# Revit family: NBS_DudleyIndustriesLimited_HndDryrs_ModuloSlimlineBehindTheMirrorHandHygieneSystemHandDryer
name_source: partatom
category: Specialty Equipment
units: mm (PartAtom-declared; Revit-internal decimal feet)

## family parameters
Always vertical = Yes
Cut with Voids When Loaded = No
Part Type = Normal
Room Calculation Point = No
Round Connector Dimension = Use Diameter
Shared = No
Work Plane-Based = No

## types (1)
- Modulo Slimline Behind The Mirror Hand Hygiene System Hand Dryer
    Accessories = Not required.,92405BK, Modulo Slimline Base Shelf, 600 mm.,92404BK,  Modulo Slimline Base Shelf, 1200 mm
    AssetType = Fixed
    BIMObjectName = NBS_DudleyIndustriesLimited_HandDryers_ModuloSlimlineBehindTheMirrorHandHygieneSystemHandDryer
    BlankingPlates = Not required.,Required
    BodyColour = Matte black
    BodyDimensions = 388 x 328 x 173 mm
    BodyFinish = Powder coated
    BodyMaterial = Stainless steel
    Category = Pr_40_70_62_37:Hand dryers
    Color = Black
    Description = Hand dryer
    DurationUnit = year
    ElectricalSupplyFrequency = 50/60 Hz
    ElectricalSupplyPowerRating = 1.7 kW
    ElectricalSupplyRatedOperationalVoltageUe = 230 V a.c
    Features = Hands only
    Finish = Powder-coated
    Form = Warm air
    HandDryerDepth = 173 mm
    HandDryerHeight = 328 mm  [stored 1.07612 ft]
    HandDryerMaterial = NBS_DudleyIndustriesLimited_StainlessSteel_MatteBlackPowderCoated
    HandDryerWidth = 388 mm  [stored 1.27297 ft]
    IfcExportAs = IfcElectricApplianceType
    IfcExportType = HANDDRYER
    ManufacturerName = Dudley Industries Limited
    ManufacturerURL = www.dudleyindustries.com
    Material = Stainless steel
    ModelReference = ModuloSlimlineBehindTheMirrorHandHygieneSystem, HandDryer
    NBSCertification = www.nationalbimlibrary.com/cert/d02wqjjd
    Name = HandDryers_ModuloSlimlineBehindTheMirrorHandHygieneSystem, HandDryer_DudleyIndustriesLimited
    NoiseLevelAt1MMaximum = 71 dB(A)
    NominalHeight = 328 mm  [stored 1.07612 ft]
    NominalLength = 0 mm  [stored 0 ft]
    NominalWidth = 388 mm  [stored 1.27297 ft]
    Operation = Automatic
    Sensors = 100 mm range
    Shape = Rectangle
    Size = 388 x 328 x 173 mm
    ThirdPartyAccreditation = CE marked
    Uniclass2015Code = Pr_40_70_62_37
    Uniclass2015Title = Hand dryers
    Uniclass2015Version = Products v1.22
    Velocity = 28 m/s
    Version = 1
    WarrantyDescription = Three year
    WarrantyDurationParts = Three year
    WarrantyDurationUnit = year
    Weight = 6.5 kg

note: [stored X ft] marks values corroborated as IEEE doubles in the binary element streams (Revit-internal decimal feet)

## geometry (parser evidence)
native form markers: Sweep x3
no freeform markers — native parametric forms only
